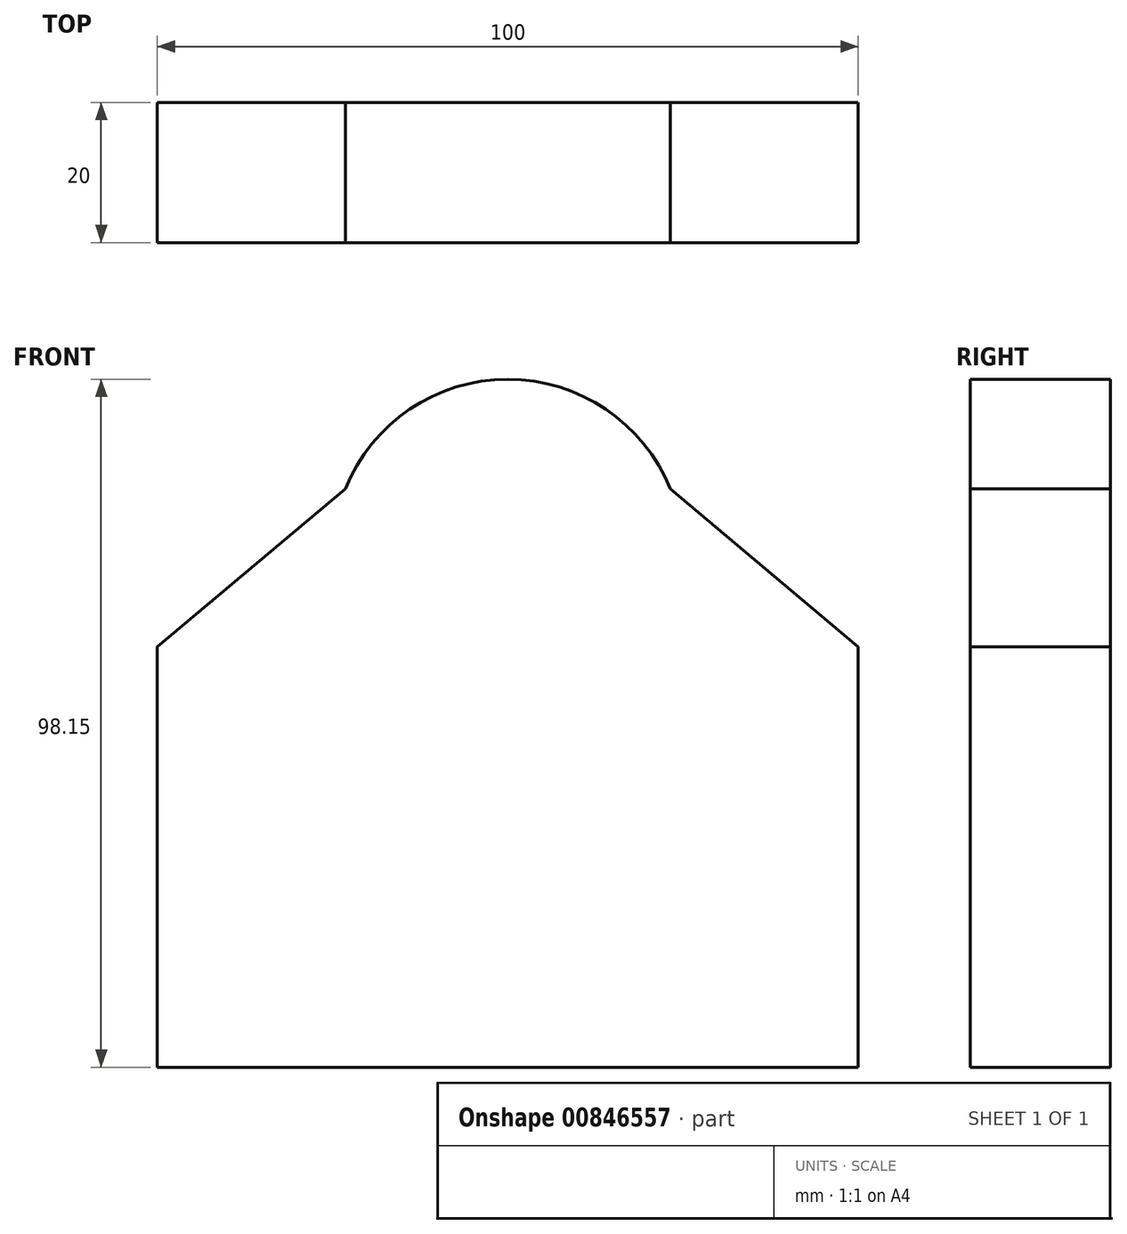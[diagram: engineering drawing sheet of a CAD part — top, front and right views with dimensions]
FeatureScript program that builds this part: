
annotation { "Feature Type Name" : "Feature", "Feature Type Description" : "" }
export const myFeature = defineFeature(function(context is Context, id is Id, definition is map)
    precondition{}
    {
        {
            var Q0;
            Q0=qCreatedBy(makeId("Front.planeOp"),FACE);
            var sketch = newSketch(context, id + "F0", { "sketchPlane" : qUnion([Q0])});
            skLineSegment(sketch, "E0", {"start": v(-52.7, -32.35) * mm, "end": v(47.3, -32.35) * mm});
            skLineSegment(sketch, "E1", {"start": v(-52.7, -32.35) * mm, "end": v(-52.7, 27.65) * mm});
            skLineSegment(sketch, "E2", {"start": v(47.3, 27.65) * mm, "end": v(47.3, -32.35) * mm});
            skLineSegment(sketch, "E3", {"start": v(47.3, 27.65) * mm, "end": v(20.5, 50.15) * mm});
            skLineSegment(sketch, "E4", {"start": v(-52.7, 27.65) * mm, "end": v(-25.88, 50.15) * mm});
            skArc(sketch, "E5", {"start": v(20.5, 50.15) * mm, "mid": v(-2.7, 65.8) * mm, "end": v(-25.88, 50.15) * mm});
            skSolve(sketch);
        }
        {
            var Q0;
            Q0=qSketchRegion(id+"F0",true);
            extrude(context, id + "F1", {"entities" : qUnion([Q0]), "depth" : 20 * mm, "offsetDistance" : 25 * mm});
        }
    });
